# Revit family: Holyoake - LF Linear Flow
name_source: partatom
category: Air Terminals
revit_build: Autodesk Revit 2018 (Build: 20190510_1515(x64)
units: mm (PartAtom-declared; Revit-internal decimal feet)

## family parameters
Cut with Voids When Loaded = No
Host = Face
Part Type = Normal
Room Calculation Point = No
Round Connector Dimension = Use Diameter
Shared = No

## types (1)
- Type 1
    D = 200 mm  [stored 0.656168 ft]
    D Cut Size = 190 mm
    D Minimum Clear Opening = 1210 mm
    D Mounting Frame = 194 mm
    D Overall Exterior = 190 mm
    Default Elevation = 1219 mm
    L = 1200 mm  [stored 3.93701 ft]
    L Blade Length = 1182 mm
    L Cut Size = 1190 mm  [stored 3.9042 ft]
    L Minimum Clear Opening = 1210 mm
    L Mounting Frame = 1194 mm  [stored 3.91732 ft]
    L Overall Exterior = 1190 mm  [stored 3.9042 ft]
    Lining Thickness = 9 mm  [stored 0.0295276 ft]
    Manufacturer = Holyoake
    Material = <By Category>
    Maximum Length = 5000 mm  [stored 16.4042 ft]
    Minimum Length = 75 mm
    Mounting = Warning: Only suitable for Wall and Ceiling applications
    Type Comments = LF Linear Flow
    URL = https://productspec.net

note: [stored X ft] marks values corroborated as IEEE doubles in the binary element streams (Revit-internal decimal feet)

## geometry (parser evidence)
native form markers: Blend x4, Sweep x13
no freeform markers — native parametric forms only
